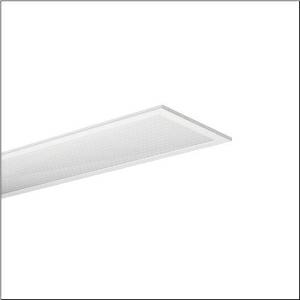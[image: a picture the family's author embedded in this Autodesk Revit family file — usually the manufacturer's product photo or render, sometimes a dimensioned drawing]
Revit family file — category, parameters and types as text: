
# Revit family: apollon_r__21_linear_51mq14wd2t12_0b39
name_source: partatom
category: Lighting Fixtures
units: mm (PartAtom-declared; Revit-internal decimal feet)

## family parameters
Cut with Voids When Loaded = No
Host = Face
Light Source = No
Part Type = Normal
Room Calculation Point = No
Round Connector Dimension = Use Diameter
Shared = No

## types (1)
- --- (1 x LED 2700 K ... 6500 K, 4200 lm, 44 W, 6500K)
    Apparent Load = 44 VA
    CIE Flux Codes = 60 87 97 100 100
    Color Rendering = 80
    Color Temperature = 6500K
    Default Elevation = 1800 mm
    Description = Apollon® 21, office luminaire, primary optical cover: micro prismatic cover, of PMMA, CAT 2 (L<= 3000cd/m²), light emission: direct distribution, primary light characteristic: symmetric, installation type: lay-in mounting, LED rated luminous flux: 4.200 lm, light colour: 8tw, colour temperature: 2700..6500K, control gear: ECG DALI, with terminal, 5-pole, mains connection: 220..240V, AC, 50/60Hz, rated input power: 44W, housing, of aluminium, coated, pure white, module: M625, length: 1.245 mm, width: 307 mm, height: 40mm, housing upper side, of sheet steel, galvanised, protection rating (complete): IP20, protection rating (lamp compartment, on room side): IP50, insulation class (complete): insulation class I (protective earthing), certification: CE, ENEC, packaging unit: 1 piece
    Height = 0 mm  [stored 0 ft]
    Lamp = 1 x LED 2700 K ... 6500 K
    Lamp Light Flux = 4200 lm
    Lamp Power = 44 W
    Lamp count = 1
    Length = 1245 mm
    Luminous efficacy = 95 lm/W
    Manufacturer = Siteco
    ModVariant = No
    Model = 51MQ14WD2T12
    Mounting Place = Ceiling
    Mounting Type = Recessed
    Number of Poles = 1
    OnlyDefault = Yes
    Power Factor = 1
    Product Name = Apollon® 21 linear
    Product group = office luminaire | ceiling recessed
    ProductGroupID = 400
    Protection Class = Protection class I
    Protection Degree = IP 20
    RLX_Detail_Level = 1
    RlxData = <blob elided: 17597 chars, md5=6ee08f64>
    Socket = socket
    Standby Power = 0 W
    System Light Flux = 4200 lm
    System Power = 44 W
    Type Comments = individual setting: CCT=6500K, colour temperature 6500K
    Type Image = l_1004243.jpg
    URL = http://relux.com
    VarID = @adj_128327
    Voltage = 0 V
    Weight = 0.00 kg
    Width = 307 mm

note: [stored X ft] marks values corroborated as IEEE doubles in the binary element streams (Revit-internal decimal feet)

## geometry (parser evidence)
native form markers: Blend x4, Sweep x13
no freeform markers — native parametric forms only
